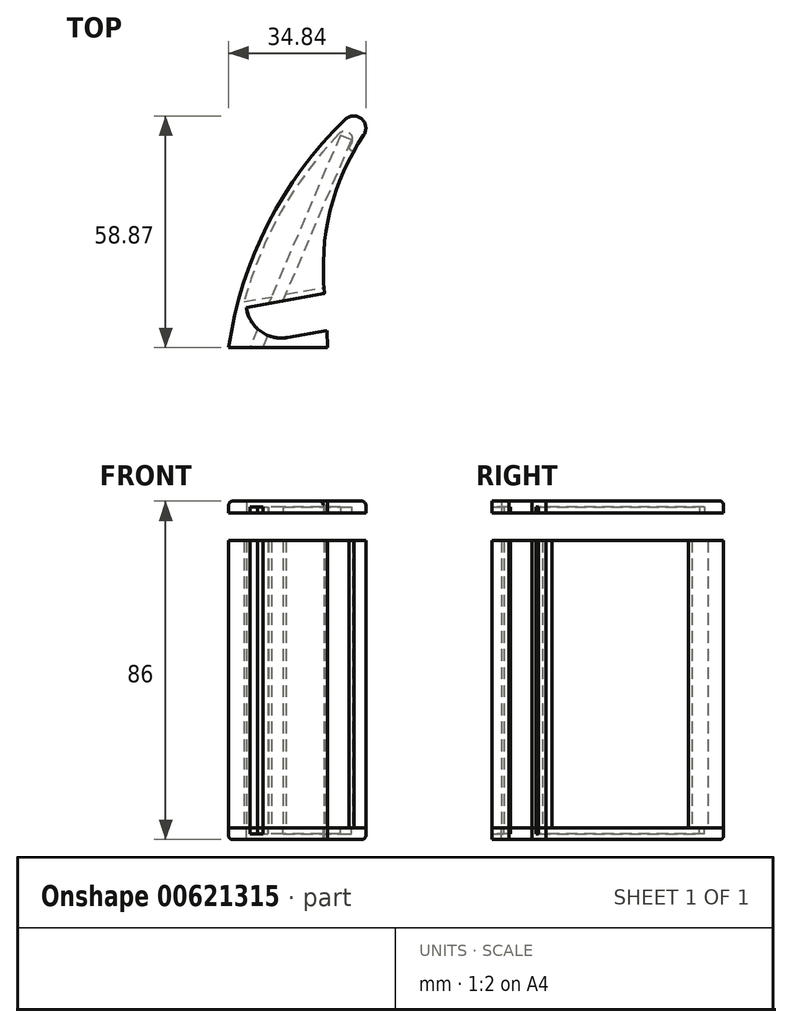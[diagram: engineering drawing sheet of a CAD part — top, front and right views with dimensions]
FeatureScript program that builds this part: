
annotation { "Feature Type Name" : "Feature", "Feature Type Description" : "" }
export const myFeature = defineFeature(function(context is Context, id is Id, definition is map)
    precondition{}
    {
        {
            var Q0;
            Q0=qCreatedBy(makeId("Top.planeOp"),FACE);
            var sketch = newSketch(context, id + "F0", { "sketchPlane" : qUnion([Q0])});
            skLineSegment(sketch, "E0", {"start": v(25.11, 0) * mm, "end": v(0, 0) * mm});
            skLineSegment(sketch, "E1", {"start": v(24.38, 13.8) * mm, "end": v(4.49, 10.24) * mm});
            skLineSegment(sketch, "E2", {"start": v(14.94, 2.56) * mm, "end": v(25.02, 4.37) * mm});
            skLineSegment(sketch, "E3", {"start": v(25.02, 4.37) * mm, "end": v(25.11, 0) * mm});
            skLineSegment(sketch, "E4", {"start": v(8.74, 0) * mm, "end": v(31.24, 52.8) * mm, "construction": true});
            skLineSegment(sketch, "E5", {"start": v(31.24, 52.8) * mm, "end": v(28.38, 54.02) * mm, "construction": true});
            skLineSegment(sketch, "E6", {"start": v(28.38, 54.02) * mm, "end": v(5.37, 0) * mm, "construction": true});
            skArc(sketch, "E7", {"start": v(29.57, 58) * mm, "mid": v(9.95, 31.46) * mm, "end": v(0, 0) * mm});
            skArc(sketch, "E8", {"start": v(34.3, 54.03) * mm, "mid": v(25.78, 34.8) * mm, "end": v(24.38, 13.8) * mm});
            skArc(sketch, "E9.filletArc", {"start": v(34.3, 54.03) * mm, "mid": v(33.72, 58.14) * mm, "end": v(29.57, 58) * mm});
            skArc(sketch, "E10", {"start": v(4.49, 10.24) * mm, "mid": v(8.06, 4.16) * mm, "end": v(14.94, 2.56) * mm});
            skSolve(sketch);
        }
        {
            var Q0;
            Q0=makeQuery(id+"F0.imprint","IMPRINT",FACE,{"disambiguationData":[TD([[makeQuery(id+"F0.imprint","IMPRINT",EDGE,{"derivedFrom":sQuery(id+"F0.wireOp",EDGE,"E0")}),-1.0]])]});
            extrude(context, id + "F1", {"entities" : qUnion([Q0]), "oppositeDirection" : true, "depth" : 3 * mm, "offsetDistance" : 25 * mm});
        }
        {
            var Q0;
            Q0=makeQuery(id+"F0.imprint","IMPRINT",FACE,{"disambiguationData":[TD([[makeQuery(id+"F0.imprint","IMPRINT",EDGE,{"derivedFrom":sQuery(id+"F0.wireOp",EDGE,"E0")}),-1.0]])]});
            var sketch = newSketch(context, id + "F2", { "sketchPlane" : qUnion([Q0])});
            skLineSegment(sketch, "E11.0", {"start": v(8.74, 0) * mm, "end": v(10.04, 3.06) * mm});
            skLineSegment(sketch, "E12.0", {"start": v(28.38, 54.02) * mm, "end": v(10.16, 11.26) * mm});
            skLineSegment(sketch, "E13.0", {"start": v(13.82, 11.91) * mm, "end": v(10.16, 11.26) * mm});
            skArc(sketch, "E14.0", {"start": v(7.38, 4.72) * mm, "mid": v(8.64, 3.77) * mm, "end": v(10.04, 3.06) * mm});
            skLineSegment(sketch, "E15", {"start": v(28.38, 54.02) * mm, "end": v(31.24, 52.8) * mm});
            skLineSegment(sketch, "E16.trimOffspring", {"start": v(13.82, 11.91) * mm, "end": v(31.24, 52.8) * mm});
            skLineSegment(sketch, "E17.trimOffspring", {"start": v(7.38, 4.72) * mm, "end": v(5.37, 0) * mm});
            skLineSegment(sketch, "E18", {"start": v(5.37, 0) * mm, "end": v(7.38, 4.72) * mm});
            skLineSegment(sketch, "E19", {"start": v(8.74, 0) * mm, "end": v(5.37, 0) * mm});
            skPoint(sketch, "E20.orphan", {"position": v(4.49, 10.24) * mm});
            skPoint(sketch, "E21.orphan", {"position": v(14.94, 2.56) * mm});
            skPoint(sketch, "E22.orphan", {"position": v(24.38, 13.8) * mm});
            skSolve(sketch);
        }
        {
            var Q0;
            Q0 = qSketchRegion(id + "F2", true);
            extrude(context, id + "F3", {"entities" : qUnion([Q0]), "operationType" : NewBodyOperationType.REMOVE, "oppositeDirection" : true, "depth" : 1.5 * mm, "offsetDistance" : 25 * mm});
        }
        {
            var Q0;
            Q0=qCreatedBy(makeId("Top.planeOp"),FACE);
            cPlane(context, id + "F4", {"entities" : qUnion([Q0]), "cplaneType" : CPlaneType.OFFSET, "offset" : 40 * mm, "width" : 150 * mm, "height" : 150 * mm});
        }
        {
            var Q0;
            Q0=makeQuery(id+"F0.imprint","IMPRINT",FACE,{"disambiguationData":[TD([[makeQuery(id+"F0.imprint","IMPRINT",EDGE,{"derivedFrom":sQuery(id+"F0.wireOp",EDGE,"E0")}),-1.0]])]});
            var sketch = newSketch(context, id + "F5", { "sketchPlane" : qUnion([Q0])});
            skArc(sketch, "E23.0", {"start": v(34.3, 54.03) * mm, "mid": v(33.03, 52.05) * mm, "end": v(31.83, 50.02) * mm});
            skLineSegment(sketch, "E24.0.0", {"start": v(4.49, 10.24) * mm, "end": v(10.16, 11.26) * mm});
            skArc(sketch, "E24.0.2", {"start": v(34.3, 54.03) * mm, "mid": v(33.72, 58.14) * mm, "end": v(29.57, 58) * mm});
            skArc(sketch, "E24.0.3", {"start": v(29.57, 58) * mm, "mid": v(9.95, 31.46) * mm, "end": v(0, 0) * mm});
            skLineSegment(sketch, "E24.0.4", {"start": v(0, 0) * mm, "end": v(5.37, 0) * mm});
            skLineSegment(sketch, "E24.0.5", {"start": v(25.11, 0) * mm, "end": v(25.02, 4.37) * mm});
            skLineSegment(sketch, "E24.0.6", {"start": v(25.02, 4.37) * mm, "end": v(14.94, 2.56) * mm});
            skArc(sketch, "E24.0.7", {"start": v(14.94, 2.56) * mm, "mid": v(12.46, 2.47) * mm, "end": v(10.04, 3.06) * mm});
            skLineSegment(sketch, "E25.0", {"start": v(10.87, 12.9) * mm, "end": v(10.16, 11.26) * mm});
            skLineSegment(sketch, "E26.0", {"start": v(8.74, 0) * mm, "end": v(10.04, 3.06) * mm});
            skLineSegment(sketch, "E27.0", {"start": v(3.93, 11.66) * mm, "end": v(10.87, 12.9) * mm});
            skArc(sketch, "E27.1", {"start": v(28.04, 54.34) * mm, "mid": v(13.3, 34.52) * mm, "end": v(3.93, 11.66) * mm});
            skPoint(sketch, "E28.visualSharp", {"position": v(48.16, 70.45) * mm});
            skArc(sketch, "E28.filletArc", {"start": v(31.2, 51.93) * mm, "mid": v(30.7, 54.55) * mm, "end": v(28.04, 54.34) * mm});
            skArc(sketch, "E29.trimOffspring", {"start": v(7.38, 4.72) * mm, "mid": v(5.43, 7.22) * mm, "end": v(4.49, 10.24) * mm});
            skLineSegment(sketch, "E30.trimOffspring", {"start": v(8.74, 0) * mm, "end": v(25.11, 0) * mm});
            skLineSegment(sketch, "E31.trimOffspring", {"start": v(7.38, 4.72) * mm, "end": v(5.37, 0) * mm});
            skPoint(sketch, "E32.orphan", {"position": v(28.38, 54.02) * mm});
            skPoint(sketch, "E33.trimOffspring.end.orphan", {"position": v(31.24, 52.8) * mm});
            skArc(sketch, "E34", {"start": v(30.57, 50.84) * mm, "mid": v(30.89, 51.39) * mm, "end": v(31.2, 51.93) * mm});
            skArc(sketch, "E35", {"start": v(31.83, 50.02) * mm, "mid": v(33.03, 52.05) * mm, "end": v(34.3, 54.03) * mm});
            skPoint(sketch, "E36.orphan", {"position": v(24.38, 13.8) * mm});
            skArc(sketch, "E37.0.1", {"start": v(24.38, 13.8) * mm, "mid": v(24.3, 14.55) * mm, "end": v(24.24, 15.3) * mm});
            skLineSegment(sketch, "E38", {"start": v(14.5, 13.56) * mm, "end": v(24.24, 15.3) * mm});
            skLineSegment(sketch, "E39", {"start": v(13.8, 11.91) * mm, "end": v(14.5, 13.56) * mm});
            skLineSegment(sketch, "E40.trimOffspring", {"start": v(13.8, 11.91) * mm, "end": v(24.38, 13.8) * mm});
            skArc(sketch, "E41", {"start": v(30.57, 50.84) * mm, "mid": v(31.02, 50.15) * mm, "end": v(31.83, 50.02) * mm});
            skSolve(sketch);
        }
        {
            var Q0;
            Q0 = qSketchRegion(id + "F5", true);
            extrude(context, id + "F6", {"entities" : qUnion([Q0]), "depth" : 73 * mm, "offsetDistance" : 25 * mm});
        }
        {
            var Q0;
            Q0=makeQuery(id+"F1.opExtrude","SWEPT_BODY",BODY,{"disambiguationData":[OSD([sQuery(id+"F0.wireOp",EDGE,"E0"),sQuery(id+"F0.wireOp",EDGE,"E1"),sQuery(id+"F0.wireOp",EDGE,"E2"),sQuery(id+"F0.wireOp",EDGE,"E3"),sQuery(id+"F0.wireOp",EDGE,"E7"),sQuery(id+"F0.wireOp",EDGE,"E8"),sQuery(id+"F0.wireOp",EDGE,"E9.filletArc"),sQuery(id+"F0.wireOp",EDGE,"E10")])]});
            var Q1;
            Q1=qCreatedBy(id+"F4.planeOp",FACE);
            mirror(context, id + "F7", {"entities" : qUnion([Q0]), "mirrorPlane" : qUnion([Q1])});
        }
        {
            var Q0;
            Q0=makeQuery(id+"F1.opExtrude","CAP_EDGE",EDGE,{"disambiguationData":[OSD([sQuery(id+"F0.wireOp",EDGE,"E7")])],"isStart":false});
            fillet(context, id + "F8", {"entities" : qUnion([Q0]), "radius" : 1 * mm, "tangentPropagation" : true, "allowEdgeOverflow" : false});
        }
        {
            var Q0;
            Q0=makeQuery(id+"F7.opPattern","COPY",EDGE,{"derivedFrom":makeQuery(id+"F1.opExtrude","CAP_EDGE",EDGE,{"disambiguationData":[OSD([sQuery(id+"F0.wireOp",EDGE,"E7")])],"isStart":false}),"instanceName":"1"});
            var Q1;
            Q1=makeQuery(id+"F7.opPattern","COPY",EDGE,{"derivedFrom":makeQuery(id+"F1.opExtrude","CAP_EDGE",EDGE,{"disambiguationData":[OSD([sQuery(id+"F0.wireOp",EDGE,"E8")])],"isStart":false}),"instanceName":"1"});
            var Q2;
            Q2=makeQuery(id+"F7.opPattern","COPY",EDGE,{"derivedFrom":makeQuery(id+"F1.opExtrude","CAP_EDGE",EDGE,{"disambiguationData":[OSD([sQuery(id+"F0.wireOp",EDGE,"E9.filletArc")])],"isStart":false}),"instanceName":"1"});
            fillet(context, id + "F9", {"entities" : qUnion([Q0, Q1, Q2]), "radius" : 1 * mm, "tangentPropagation" : true, "allowEdgeOverflow" : false});
        }
    });
